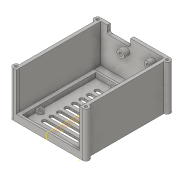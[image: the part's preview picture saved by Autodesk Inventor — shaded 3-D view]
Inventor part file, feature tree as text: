
AUTODESK INVENTOR PART (.ipt)
format: ipt  version: 2016 (Build 200138000, 138)  size: 365,568 bytes
history: native  units: in
note: dims shown in document units (in); Inventor stores cm internally (conversion verified against a paired STEP export)
features: sketch x28, extrude x27, pattern_linear x4, fillet x2, plane x1
ambient origin geometry x8: Origin, YZ Plane, XZ Plane, XY Plane, X Axis, Y Axis, Z Axis, Center Point
bodies: Solid1 (feature_tree)
feature tree (62):
  extrude  "Extrusion1"  Depth=3.3465in
  extrude  "Extrusion2"  Depth=2.0945in
  plane  "Work Plane1"
  extrude  "Extrusion4"  Depth=0.0787in
  extrude  "Extrusion5"  Depth=0.1969in
  extrude  "Extrusion6"  Depth=0.1181in TaperAngle=0.0deg
  extrude  "Extrusion7"  Depth=0.3937in TaperAngle=0.0deg
  extrude  "Extrusion8"  Depth=0.1181in
  extrude  "Extrusion9"  Depth=0.1181in TaperAngle=0.0deg
  extrude  "Extrusion10"  Depth=0.3937in TaperAngle=0.0deg
  extrude  "Extrusion11"  Depth=0.1181in TaperAngle=0.0deg
  extrude  "Extrusion12"  Depth=0.3937in TaperAngle=0.0deg
  fillet  "Fillet1"  Radius=1.378in
  pattern_linear  "Rectangular Pattern1"  Count1=8 Spacing1=0.2756in
  pattern_linear  "Rectangular Pattern2"  Count1=8 Spacing1=0.2756in
  extrude  "Extrusion13"  Depth=2.5591in
  sketch  "Sketch14"  dims[d48=0.3937in d49=0.0in]
  extrude  "Extrusion14"  Depth=0.1969in TaperAngle=0.0deg
  extrude  "Extrusion15"  Depth=0.1181in
  extrude  "Extrusion16"  Depth=0.1181in
  extrude  "Extrusion17"  Depth=0.1181in
  extrude  "Extrusion18"  Depth=0.1772in TaperAngle=0.0deg
  extrude  "Extrusion19"  Depth=0.1772in TaperAngle=0.0deg
  extrude  "Extrusion20"  Depth=0.1969in TaperAngle=0.0deg
  extrude  "Extrusion21"  Depth=0.1969in TaperAngle=0.0deg
  extrude  "Extrusion22"  Depth=0.0787in
  extrude  "Extrusion23"  Depth=0.3937in TaperAngle=0.0deg
  fillet  "Fillet2"  Radius=0.1772in
  extrude  "Extrusion24"  Depth=0.3937in TaperAngle=0.0deg
  extrude  "Extrusion25"  Depth=1.6535in
  extrude  "Extrusion26"  Depth=0.0984in
  extrude  "Extrusion27"  Depth=1.6535in TaperAngle=0.0deg
  pattern_linear  "Rectangular Pattern3"  Count1=2 Spacing1=2.9828in
  extrude  "Extrusion28"  Depth=2.5591in
  pattern_linear  "Rectangular Pattern4"  [2 undecoded]
  sketch  "Sketch1"  dims[d0=2.5591in d1=3.3465in]
  sketch  "Sketch2"  dims[d2=0.0787in d3=0.0in d4=2.0945in]
  sketch  "Sketch4"  dims[d5=2.7047in d6=0.0787in]
  sketch  "Sketch5"  dims[d7=0.1969in d8=0.0in d13=1.0472in]
  sketch  "Sketch6"  dims[d17=0.1969in d18=0.1181in d19=0.0in]
  sketch  "Sketch7"  dims[d20=0.126in d21=0.3937in d22=0.0in]
  sketch  "Sketch8"  dims[d26=0.1181in d27=0.0in d28=0.126in]
  sketch  "Sketch9"  dims[d29=0.3937in d30=0.0in d33=0.1181in d34=0.0in]
  sketch  "Sketch10"  dims[d35=0.126in d36=0.3937in d37=0.0in]
  sketch  "Sketch11"  dims[d40=0.1969in d41=0.1181in d42=0.0in]
  sketch  "Sketch12"  dims[d43=0.126in d44=0.3937in d45=0.0in d46=1.378in]
  sketch  "Sketch13"  dims[d47=0.1575in]
  sketch  "Sketch15"  dims[d50=0.0787in d51=3.1496in d53=0.2756in d54=3.1496in d56=0.2756in]
  sketch  "Sketch18"  dims[d57=0.0197in d58=0.0in d59=2.5591in]
  sketch  "Sketch19"  dims[d60=0.1271in d61=0.1969in d62=0.0in]
  sketch  "Sketch20"  dims[d63=2.5591in d64=0.1181in]
  sketch  "Sketch21"  dims[d65=1.5748in d66=0.0in d67=0.1181in]
  sketch  "Sketch22"  dims[d68=1.5748in d69=0.0in d70=0.1181in]
  sketch  "Sketch24"  dims[d71=1.5748in d72=0.0in d73=0.1772in d74=0.0in]
  sketch  "Sketch25"  dims[d75=0.1772in d76=0.0in d77=0.0004in d78=0.0in]
  sketch  "Sketch26"  dims[d79=0.2756in d80=0.1969in d81=0.0in]
  sketch  "Sketch27"  dims[d84=0.2756in d85=0.1969in d86=0.0in]
  sketch  "Sketch28"  dims[d87=0.1969in d88=0.0in d89=0.0787in]
  sketch  "Sketch30"  dims[d90=0.126in d91=0.3937in d92=0.0in d93=0.1772in d94=0.0in]
  sketch  "Sketch31"  dims[d95=0.126in d96=0.3937in d97=0.0in]
  sketch  "Sketch32"  dims[d98=1.6535in d99=0.0in d100=0.7874in d102=2.9828in]
  sketch  "Sketch33"  dims[d103=0.7874in d105=2.5591in d106=0.0984in d107=1.6535in d108=0.0in d109=0.7874in d111=2.9828in d112=0.7874in d114=2.5591in]
note: 2 required parameter values undecoded (feature->parameter linkage not recoverable at this tier; creation-order binding heuristic only, values carry confidence <= 0.55)
